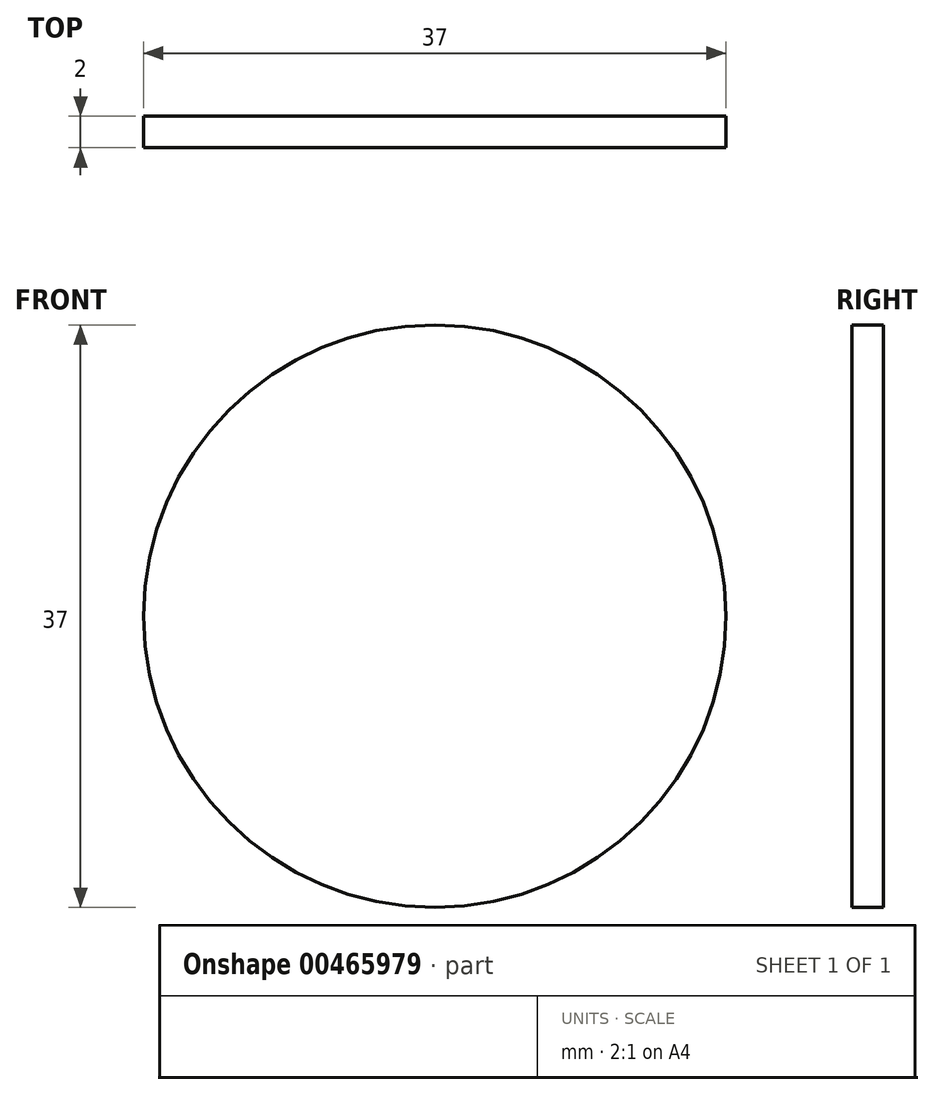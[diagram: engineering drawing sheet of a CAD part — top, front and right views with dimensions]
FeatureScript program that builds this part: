
annotation { "Feature Type Name" : "Feature", "Feature Type Description" : "" }
export const myFeature = defineFeature(function(context is Context, id is Id, definition is map)
    precondition{}
    {
        {
            var Q0;
            Q0=qCreatedBy(makeId("Front.planeOp"),FACE);
            var sketch = newSketch(context, id + "F0", { "sketchPlane" : qUnion([Q0]), "disableImprinting" : false});
            skCircle(sketch, "E0", {"center": v(0, 0) * mm, "radius": 18.5 * mm});
            skCircle(sketch, "E1", {"center": v(78, 0) * mm, "radius": 2.06 * mm});
            skSolve(sketch);
        }
        {
            var Q0;
            Q0=makeQuery(id+"F0.imprint","IMPRINT",FACE,{"disambiguationData":[TD([[makeQuery(id+"F0.imprint","IMPRINT",EDGE,{"derivedFrom":sQuery(id+"F0.wireOp",EDGE,"E0")}),1.0]])]});
            extrude(context, id + "F1", {"entities" : qUnion([Q0]), "flatOperationType" : FlatOperationType.REMOVE, "thickness" : 5 * mm, "thickness2" : 0 * mm, "thickness1" : 5 * mm, "depth" : 2 * mm, "offsetDistance" : 25.4 * mm, "startOffsetDistance" : 25 * mm, "startOffsetBound" : StartOffsetType.BLIND, "domain" : OperationDomain.MODEL});
        }
    });
